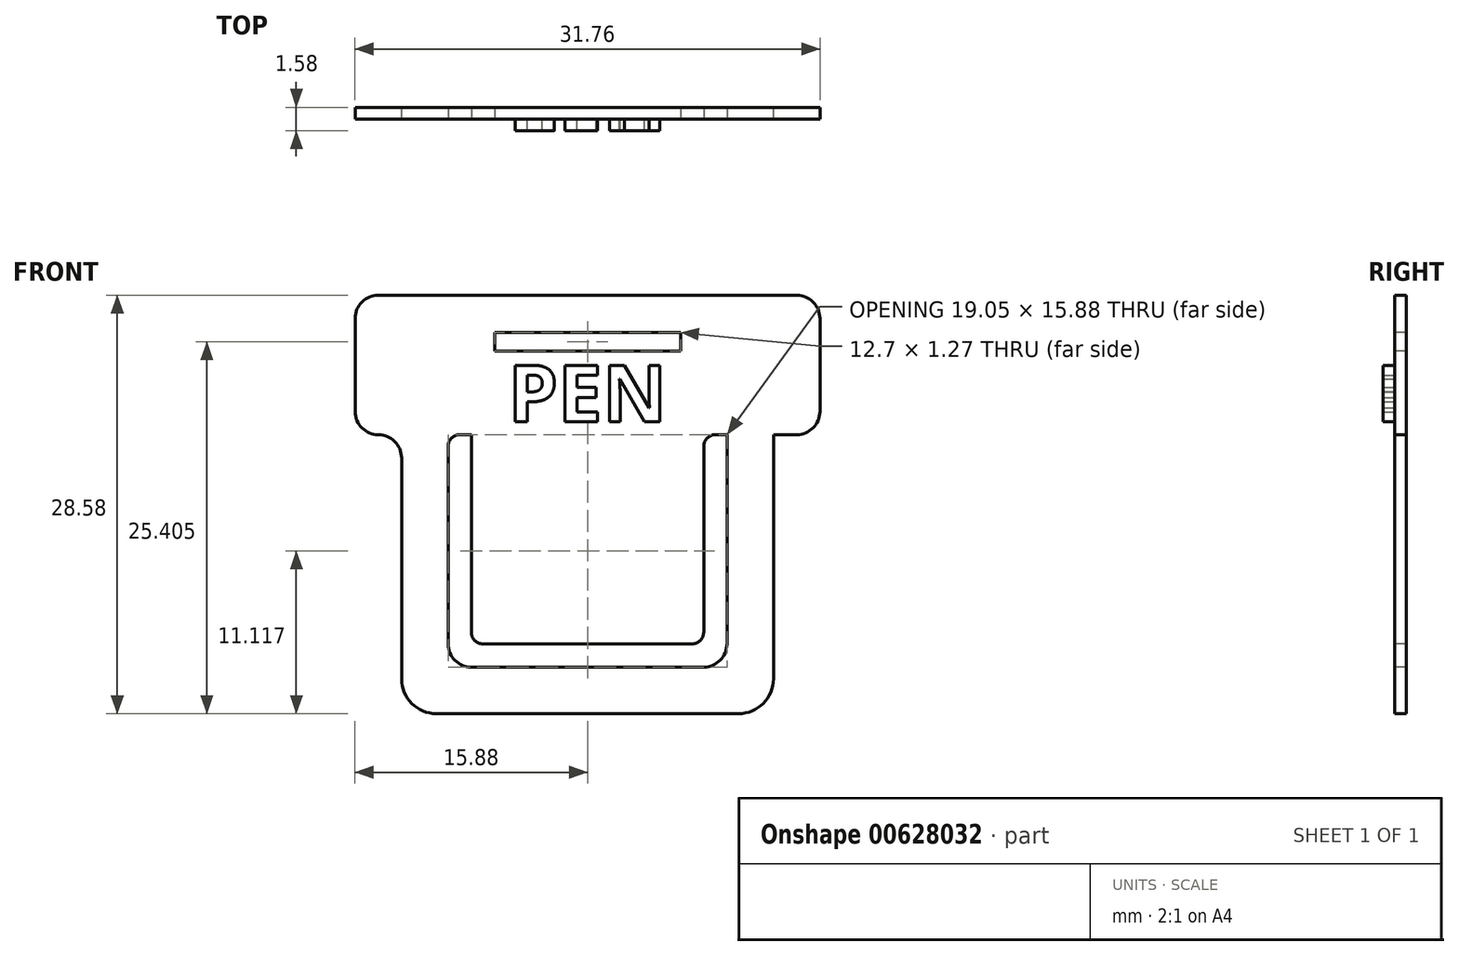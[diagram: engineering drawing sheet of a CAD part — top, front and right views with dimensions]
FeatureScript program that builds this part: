
annotation { "Feature Type Name" : "Feature", "Feature Type Description" : "" }
export const myFeature = defineFeature(function(context is Context, id is Id, definition is map)
    precondition{}
    {
        {
            var Q0;
            Q0=qCreatedBy(makeId("Front.planeOp"),FACE);
            var sketch = newSketch(context, id + "F0", { "sketchPlane" : qUnion([Q0])});
            skLineSegment(sketch, "E0.bottom", {"start": v(12.7, 9.53) * mm, "end": v(-12.7, 9.53) * mm});
            skLineSegment(sketch, "E0.top", {"start": v(12.7, -9.53) * mm, "end": v(-12.7, -9.53) * mm});
            skLineSegment(sketch, "E0.left", {"start": v(12.7, 9.53) * mm, "end": v(12.7, -9.53) * mm});
            skLineSegment(sketch, "E0.right", {"start": v(-12.7, 9.53) * mm, "end": v(-12.7, -9.53) * mm});
            skPoint(sketch, "E0.middle", {"position": v(0, 0) * mm});
            skSolve(sketch);
        }
        {
            var Q0;
            Q0=makeQuery(id+"F0.imprint","IMPRINT",FACE,{"disambiguationData":[TD([[makeQuery(id+"F0.imprint","IMPRINT",EDGE,{"derivedFrom":sQuery(id+"F0.wireOp",EDGE,"E0.bottom")}),1.0]])]});
            extrude(context, id + "F1", {"entities" : qUnion([Q0]), "depth" : 0.8 * mm, "offsetDistance" : 25.4 * mm});
        }
        {
            var Q0;
            Q0=makeQuery(id+"F1.opExtrude","SWEPT_EDGE",EDGE,{"disambiguationData":[OSD([sQuery(id+"F0.wireOp",EDGE,"E0.top"),sQuery(id+"F0.wireOp",EDGE,"E0.left")])]});
            var Q1;
            Q1=makeQuery(id+"F1.opExtrude","SWEPT_EDGE",EDGE,{"disambiguationData":[OSD([sQuery(id+"F0.wireOp",EDGE,"E0.top"),sQuery(id+"F0.wireOp",EDGE,"E0.right")])]});
            fillet(context, id + "F2", {"entities" : qUnion([Q0, Q1]), "radius" : 2.38 * mm, "tangentPropagation" : true, "allowEdgeOverflow" : false});
        }
        {
            var Q0;
            Q0=makeQuery(id+"F1.opExtrude","CAP_FACE",FACE,{"disambiguationData":[OSD([sQuery(id+"F0.wireOp",EDGE,"E0.bottom"),sQuery(id+"F0.wireOp",EDGE,"E0.top"),sQuery(id+"F0.wireOp",EDGE,"E0.left"),sQuery(id+"F0.wireOp",EDGE,"E0.right")])],"isStart":false});
            var sketch = newSketch(context, id + "F3", { "sketchPlane" : qUnion([Q0])});
            skLineSegment(sketch, "E1.bottom", {"start": v(9.52, 9.53) * mm, "end": v(-9.53, 9.53) * mm});
            skLineSegment(sketch, "E1.top", {"start": v(9.53, -6.35) * mm, "end": v(-9.53, -6.35) * mm});
            skLineSegment(sketch, "E1.left", {"start": v(9.52, 9.53) * mm, "end": v(9.53, -6.35) * mm});
            skLineSegment(sketch, "E1.right", {"start": v(-9.53, 9.53) * mm, "end": v(-9.52, -6.35) * mm});
            skPoint(sketch, "E1.middle", {"position": v(0, 0) * mm});
            skSolve(sketch);
        }
        {
            var Q0;
            Q0=makeQuery(id+"F3.imprint","IMPRINT",FACE,{"disambiguationData":[TD([[makeQuery(id+"F3.imprint","IMPRINT",EDGE,{"derivedFrom":sQuery(id+"F3.wireOp",EDGE,"E1.bottom")}),1.0]])]});
            extrude(context, id + "F4", {"entities" : qUnion([Q0]), "operationType" : NewBodyOperationType.REMOVE, "oppositeDirection" : true, "depth" : 4.93 * mm, "offsetDistance" : 25.4 * mm});
        }
        {
            var Q0;
            Q0=makeQuery(id+"F1.opExtrude","CAP_FACE",FACE,{"disambiguationData":[OSD([sQuery(id+"F0.wireOp",EDGE,"E0.bottom"),sQuery(id+"F0.wireOp",EDGE,"E0.top"),sQuery(id+"F0.wireOp",EDGE,"E0.left"),sQuery(id+"F0.wireOp",EDGE,"E0.right")])],"isStart":false});
            var sketch = newSketch(context, id + "F5", { "sketchPlane" : qUnion([Q0])});
            skLineSegment(sketch, "E2.bottom", {"start": v(-15.88, 9.53) * mm, "end": v(15.87, 9.53) * mm});
            skLineSegment(sketch, "E2.top", {"start": v(-15.88, 19.05) * mm, "end": v(15.87, 19.05) * mm});
            skLineSegment(sketch, "E2.left", {"start": v(-15.88, 9.53) * mm, "end": v(-15.88, 19.05) * mm});
            skLineSegment(sketch, "E2.right", {"start": v(15.87, 9.53) * mm, "end": v(15.87, 19.05) * mm});
            skLineSegment(sketch, "E3.bottom", {"start": v(-6.35, 16.51) * mm, "end": v(6.35, 16.51) * mm});
            skLineSegment(sketch, "E3.top", {"start": v(-6.35, 15.24) * mm, "end": v(6.35, 15.24) * mm});
            skLineSegment(sketch, "E3.left", {"start": v(-6.35, 16.51) * mm, "end": v(-6.35, 15.24) * mm});
            skLineSegment(sketch, "E3.right", {"start": v(6.35, 16.51) * mm, "end": v(6.35, 15.24) * mm});
            skSolve(sketch);
        }
        {
            var Q0;
            Q0=makeQuery(id+"F5.imprint","IMPRINT",FACE,{"disambiguationData":[TD([[makeQuery(id+"F5.imprint","IMPRINT",EDGE,{"derivedFrom":sQuery(id+"F5.wireOp",EDGE,"E2.top")}),-1.0]])]});
            extrude(context, id + "F6", {"entities" : qUnion([Q0]), "operationType" : NewBodyOperationType.ADD, "oppositeDirection" : true, "depth" : 0.8 * mm, "offsetDistance" : 25.4 * mm});
        }
        {
            var Q0;
            Q0=makeQuery(id+"F6.opExtrude","SWEPT_EDGE",EDGE,{"disambiguationData":[OSD([sQuery(id+"F5.wireOp",EDGE,"E2.top"),sQuery(id+"F5.wireOp",EDGE,"E2.left")])]});
            var Q1;
            Q1=makeQuery(id+"F6.opExtrude","SWEPT_EDGE",EDGE,{"disambiguationData":[OSD([sQuery(id+"F5.wireOp",EDGE,"E2.top"),sQuery(id+"F5.wireOp",EDGE,"E2.right")])]});
            var Q2;
            Q2=makeQuery(id+"F6.opExtrude","SWEPT_EDGE",EDGE,{"disambiguationData":[OSD([sQuery(id+"F5.wireOp",EDGE,"E2.bottom"),sQuery(id+"F5.wireOp",EDGE,"E2.right")])]});
            var Q3;
            Q3=makeQuery(id+"F1.opExtrude","SWEPT_EDGE",EDGE,{"disambiguationData":[OSD([sQuery(id+"F0.wireOp",EDGE,"E0.bottom"),sQuery(id+"F0.wireOp",EDGE,"E0.left")])]});
            var Q4;
            Q4=makeQuery(id+"F6.opExtrude","SWEPT_EDGE",EDGE,{"disambiguationData":[OSD([sQuery(id+"F5.wireOp",EDGE,"E2.bottom"),sQuery(id+"F5.wireOp",EDGE,"E2.left")])]});
            var Q5;
            Q5=makeQuery(id+"F1.opExtrude","SWEPT_EDGE",EDGE,{"disambiguationData":[OSD([sQuery(id+"F0.wireOp",EDGE,"E0.bottom"),sQuery(id+"F0.wireOp",EDGE,"E0.right")])]});
            fillet(context, id + "F7", {"entities" : qUnion([Q0, Q1, Q2, Q3, Q4, Q5]), "radius" : 1.59 * mm, "tangentPropagation" : true, "allowEdgeOverflow" : false});
        }
        {
            var Q0;
            Q0=makeQuery(id+"F4.boolean.opBoolean","COPY",EDGE,{"derivedFrom":makeQuery(id+"F4.opExtrude","SWEPT_EDGE",EDGE,{"disambiguationData":[OSD([sQuery(id+"F3.wireOp",EDGE,"E1.top"),sQuery(id+"F3.wireOp",EDGE,"E1.right")])]})});
            var Q1;
            Q1=makeQuery(id+"F4.boolean.opBoolean","COPY",EDGE,{"derivedFrom":makeQuery(id+"F4.opExtrude","SWEPT_EDGE",EDGE,{"disambiguationData":[OSD([sQuery(id+"F3.wireOp",EDGE,"E1.top"),sQuery(id+"F3.wireOp",EDGE,"E1.left")])]})});
            fillet(context, id + "F8", {"entities" : qUnion([Q0, Q1]), "radius" : 1.59 * mm, "tangentPropagation" : true, "allowEdgeOverflow" : false});
        }
        {
            var Q0;
            Q0=makeQuery(id+"F6.boolean.opBoolean","MERGE",FACE,{"derivedFrom":[makeQuery(id+"F1.opExtrude","CAP_FACE",FACE,{"disambiguationData":[OSD([sQuery(id+"F0.wireOp",EDGE,"E0.bottom"),sQuery(id+"F0.wireOp",EDGE,"E0.top"),sQuery(id+"F0.wireOp",EDGE,"E0.left"),sQuery(id+"F0.wireOp",EDGE,"E0.right")])],"isStart":false}),makeQuery(id+"F6.opExtrude","CAP_FACE",FACE,{"disambiguationData":[OSD([sQuery(id+"F5.wireOp",EDGE,"E2.bottom"),sQuery(id+"F5.wireOp",EDGE,"E2.top"),sQuery(id+"F5.wireOp",EDGE,"E2.left"),sQuery(id+"F5.wireOp",EDGE,"E2.right")])],"isStart":true})]});
            var sketch = newSketch(context, id + "F9", { "sketchPlane" : qUnion([Q0])});
            skLineSegment(sketch, "E4.bottom", {"start": v(-7.94, 9.53) * mm, "end": v(7.94, 9.53) * mm});
            skLineSegment(sketch, "E4.top", {"start": v(-7.94, -4.76) * mm, "end": v(7.94, -4.76) * mm});
            skLineSegment(sketch, "E4.left", {"start": v(-7.94, 9.53) * mm, "end": v(-7.94, -4.76) * mm});
            skLineSegment(sketch, "E4.right", {"start": v(7.94, 9.53) * mm, "end": v(7.94, -4.76) * mm});
            skSolve(sketch);
        }
        {
            var Q0;
            Q0=makeQuery(id+"F9.imprint","IMPRINT",FACE,{"disambiguationData":[TD([[makeQuery(id+"F9.imprint","IMPRINT",EDGE,{"derivedFrom":sQuery(id+"F9.wireOp",EDGE,"E4.bottom")}),1.0]])]});
            extrude(context, id + "F10", {"entities" : qUnion([Q0]), "operationType" : NewBodyOperationType.ADD, "oppositeDirection" : true, "depth" : 0.8 * mm, "offsetDistance" : 25.4 * mm});
        }
        {
            var Q0;
            Q0=makeQuery(id+"F10.opExtrude","SWEPT_EDGE",EDGE,{"disambiguationData":[OSD([sQuery(id+"F5.wireOp",EDGE,"E2.bottom"),sQuery(id+"F9.wireOp",EDGE,"E4.bottom"),sQuery(id+"F9.wireOp",EDGE,"E4.left")])]});
            var Q1;
            Q1=makeQuery(id+"F4.boolean.opBoolean","COPY",EDGE,{"derivedFrom":makeQuery(id+"F4.opExtrude","SWEPT_EDGE",EDGE,{"disambiguationData":[OSD([sQuery(id+"F0.wireOp",EDGE,"E0.bottom"),sQuery(id+"F3.wireOp",EDGE,"E1.bottom"),sQuery(id+"F3.wireOp",EDGE,"E1.right")])]})});
            var Q2;
            Q2=makeQuery(id+"F10.opExtrude","SWEPT_EDGE",EDGE,{"disambiguationData":[OSD([sQuery(id+"F5.wireOp",EDGE,"E2.bottom"),sQuery(id+"F9.wireOp",EDGE,"E4.bottom"),sQuery(id+"F9.wireOp",EDGE,"E4.right")])]});
            var Q3;
            Q3=makeQuery(id+"F4.boolean.opBoolean","COPY",EDGE,{"derivedFrom":makeQuery(id+"F4.opExtrude","SWEPT_EDGE",EDGE,{"disambiguationData":[OSD([sQuery(id+"F0.wireOp",EDGE,"E0.bottom"),sQuery(id+"F3.wireOp",EDGE,"E1.bottom"),sQuery(id+"F3.wireOp",EDGE,"E1.left")])]})});
            fillet(context, id + "F11", {"entities" : qUnion([Q0, Q1, Q2, Q3]), "radius" : 0.8 * mm, "tangentPropagation" : true, "allowEdgeOverflow" : false});
        }
        {
            var Q0;
            Q0=makeQuery(id+"F10.opExtrude","SWEPT_EDGE",EDGE,{"disambiguationData":[OSD([sQuery(id+"F9.wireOp",EDGE,"E4.top"),sQuery(id+"F9.wireOp",EDGE,"E4.left")])]});
            var Q1;
            Q1=makeQuery(id+"F10.opExtrude","SWEPT_EDGE",EDGE,{"disambiguationData":[OSD([sQuery(id+"F9.wireOp",EDGE,"E4.top"),sQuery(id+"F9.wireOp",EDGE,"E4.right")])]});
            fillet(context, id + "F12", {"entities" : qUnion([Q0, Q1]), "radius" : 0.8 * mm, "tangentPropagation" : true, "allowEdgeOverflow" : false});
        }
        {
            var Q0;
            Q0=makeQuery(id+"F10.boolean.opBoolean","MERGE",FACE,{"derivedFrom":[makeQuery(id+"F6.boolean.opBoolean","MERGE",FACE,{"derivedFrom":[makeQuery(id+"F1.opExtrude","CAP_FACE",FACE,{"disambiguationData":[OSD([sQuery(id+"F0.wireOp",EDGE,"E0.bottom"),sQuery(id+"F0.wireOp",EDGE,"E0.top"),sQuery(id+"F0.wireOp",EDGE,"E0.left"),sQuery(id+"F0.wireOp",EDGE,"E0.right")])],"isStart":false}),makeQuery(id+"F6.opExtrude","CAP_FACE",FACE,{"disambiguationData":[OSD([sQuery(id+"F5.wireOp",EDGE,"E2.bottom"),sQuery(id+"F5.wireOp",EDGE,"E2.top"),sQuery(id+"F5.wireOp",EDGE,"E2.left"),sQuery(id+"F5.wireOp",EDGE,"E2.right"),sQuery(id+"F5.wireOp",EDGE,"E3.bottom"),sQuery(id+"F5.wireOp",EDGE,"E3.top"),sQuery(id+"F5.wireOp",EDGE,"E3.left"),sQuery(id+"F5.wireOp",EDGE,"E3.right")])],"isStart":true})]}),makeQuery(id+"F10.opExtrude","CAP_FACE",FACE,{"disambiguationData":[OSD([sQuery(id+"F9.wireOp",EDGE,"E4.bottom"),sQuery(id+"F9.wireOp",EDGE,"E4.top"),sQuery(id+"F9.wireOp",EDGE,"E4.left"),sQuery(id+"F9.wireOp",EDGE,"E4.right")])],"isStart":true})]});
            var sketch = newSketch(context, id + "F13", { "sketchPlane" : qUnion([Q0])});
            skText(sketch, "E5", { "text": "PEN", "fontName": "OpenSans-Bold.ttf"});
            skPoint(sketch, "E5.firstSnap0", {"position": v(-15.88, 14.29) * mm});
            const initialGuessF13  = {"E5": [-0.00542, 0.0104, 1, 0, 0.0039]};
            skSetInitialGuess(sketch, initialGuessF13);
            skSolve(sketch);
        }
        {
            var Q0;
            Q0 = qSketchRegion(id + "F13", true);
            extrude(context, id + "F14", {"entities" : qUnion([Q0]), "operationType" : NewBodyOperationType.ADD, "depth" : 0.79 * mm, "offsetDistance" : 25.4 * mm});
        }
    });
